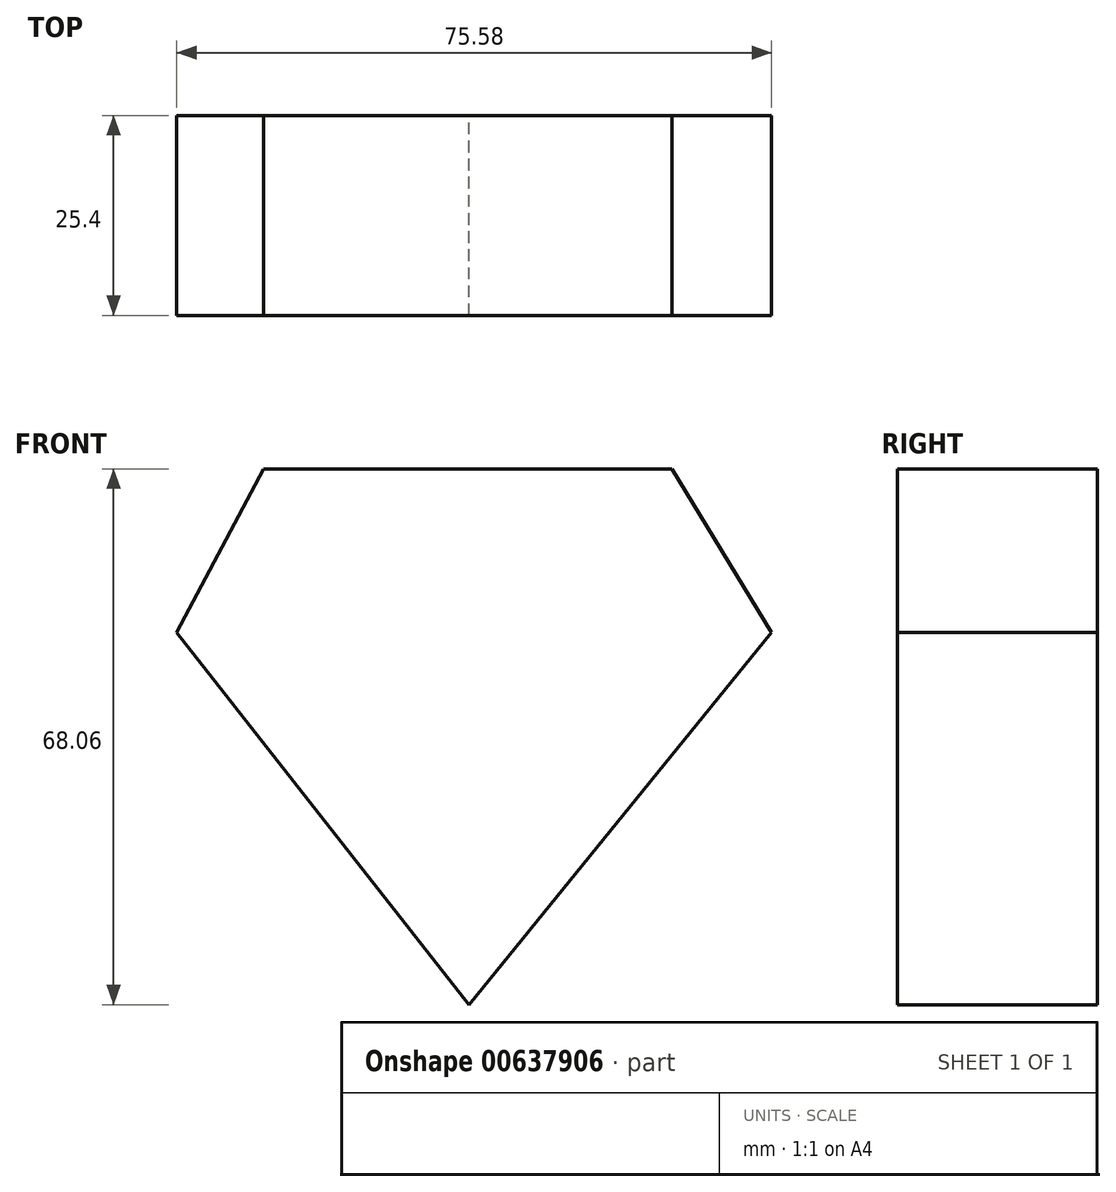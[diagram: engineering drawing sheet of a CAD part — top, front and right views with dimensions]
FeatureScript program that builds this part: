
annotation { "Feature Type Name" : "Feature", "Feature Type Description" : "" }
export const myFeature = defineFeature(function(context is Context, id is Id, definition is map)
    precondition{}
    {
        {
            var Q0;
            Q0=qCreatedBy(makeId("Front.planeOp"),FACE);
            var sketch = newSketch(context, id + "F0", { "sketchPlane" : qUnion([Q0])});
            skLineSegment(sketch, "E0", {"start": v(75.58, 0) * mm, "end": v(62.91, 20.77) * mm});
            skLineSegment(sketch, "E1", {"start": v(62.91, 20.77) * mm, "end": v(16.65, 20.77) * mm});
            skLineSegment(sketch, "E2", {"start": v(16.65, 20.77) * mm, "end": v(11.05, 20.77) * mm});
            skLineSegment(sketch, "E3", {"start": v(11.05, 20.77) * mm, "end": v(0, 0) * mm});
            skLineSegment(sketch, "E4", {"start": v(0, 0) * mm, "end": v(37.13, -47.3) * mm});
            skLineSegment(sketch, "E5", {"start": v(37.13, -47.3) * mm, "end": v(75.58, 0) * mm});
            skLineSegment(sketch, "E6", {"start": v(11.05, 20.77) * mm, "end": v(37.13, -47.3) * mm});
            skLineSegment(sketch, "E7", {"start": v(62.91, 20.77) * mm, "end": v(37.13, -47.3) * mm});
            skLineSegment(sketch, "E8", {"start": v(19, 0) * mm, "end": v(34.92, 20.77) * mm});
            skLineSegment(sketch, "E9", {"start": v(34.92, 20.77) * mm, "end": v(55.04, 0) * mm});
            skLineSegment(sketch, "E10", {"start": v(55.04, 0) * mm, "end": v(0, 0) * mm});
            skLineSegment(sketch, "E11", {"start": v(75.58, 0) * mm, "end": v(71.1, -5.5) * mm});
            skLineSegment(sketch, "E12", {"start": v(71.1, -5.5) * mm, "end": v(75.58, 0) * mm});
            skLineSegment(sketch, "E13", {"start": v(55.04, 0) * mm, "end": v(75.58, 0) * mm});
            skSolve(sketch);
        }
        {
            var Q0;
            Q0 = qSketchRegion(id + "F0", true);
            extrude(context, id + "F1", {"entities" : qUnion([Q0]), "depth" : 25.4 * mm, "offsetDistance" : 25.4 * mm});
        }
    });
